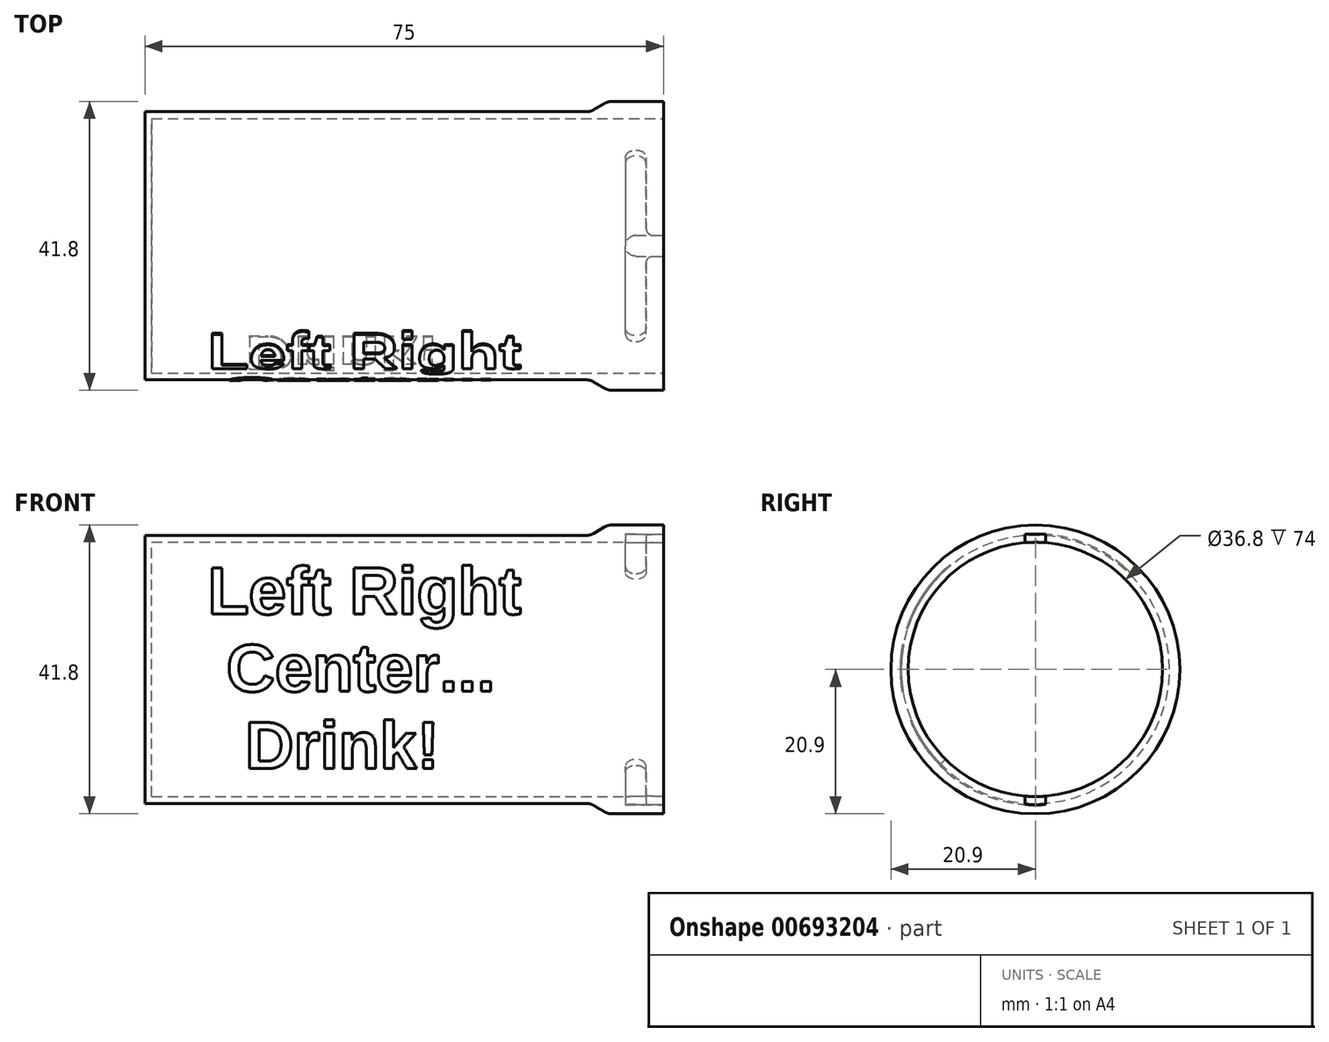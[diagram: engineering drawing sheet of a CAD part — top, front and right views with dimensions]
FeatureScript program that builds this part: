
annotation { "Feature Type Name" : "Feature", "Feature Type Description" : "" }
export const myFeature = defineFeature(function(context is Context, id is Id, definition is map)
    precondition{}
    {
        {
            var Q0;
            Q0=qCreatedBy(makeId("Front.planeOp"),FACE);
            var sketch = newSketch(context, id + "F0", { "sketchPlane" : qUnion([Q0])});
            skLineSegment(sketch, "E0", {"start": v(0, 0) * mm, "end": v(0, 19.4) * mm});
            skLineSegment(sketch, "E1", {"start": v(0, 19.4) * mm, "end": v(64.4, 19.4) * mm});
            skLineSegment(sketch, "E2", {"start": v(67, 20.9) * mm, "end": v(75, 20.9) * mm});
            skLineSegment(sketch, "E3", {"start": v(75, 20.9) * mm, "end": v(75, 18.4) * mm});
            skLineSegment(sketch, "E4", {"start": v(68.5, 18.4) * mm, "end": v(1, 18.4) * mm});
            skLineSegment(sketch, "E5", {"start": v(1, 18.4) * mm, "end": v(1, 0) * mm});
            skLineSegment(sketch, "E6", {"start": v(1, 0) * mm, "end": v(0, 0) * mm});
            skLineSegment(sketch, "E7", {"start": v(68.5, 18.4) * mm, "end": v(75, 18.4) * mm});
            skLineSegment(sketch, "E8", {"start": v(67, 20.9) * mm, "end": v(64.4, 19.4) * mm});
            skSolve(sketch);
        }
        {
            var Q0;
            Q0=makeQuery(id+"F0.imprint","IMPRINT",FACE,{"disambiguationData":[TD([[makeQuery(id+"F0.imprint","IMPRINT",EDGE,{"derivedFrom":sQuery(id+"F0.wireOp",EDGE,"E0")}),-1.0]])]});
            var Q1;
            Q1=sQuery(id+"F0.wireOp",EDGE,"E6");
            revolve(context, id + "F1", {"surfaceOperationType" : NewSurfaceOperationType.NEW, "entities" : qUnion([Q0]), "axis" : qUnion([Q1]), "revolveType" : RevolveType.FULL});
        }
        {
            var Q0;
            Q0=makeQuery(id+"F1.opRevolve","SWEPT_EDGE",EDGE,{"disambiguationData":[OSD([sQuery(id+"F0.wireOp",EDGE,"E2"),sQuery(id+"F0.wireOp",EDGE,"E8")])]});
            var Q1;
            Q1=makeQuery(id+"F1.opRevolve","SWEPT_EDGE",EDGE,{"disambiguationData":[OSD([sQuery(id+"F0.wireOp",EDGE,"E1"),sQuery(id+"F0.wireOp",EDGE,"E8")])]});
            fillet(context, id + "F2", {"entities" : qUnion([Q0, Q1]), "radius" : 2 * mm, "tangentPropagation" : true, "allowEdgeOverflow" : false});
        }
        {
            var Q0;
            Q0=makeQuery(id+"F1.opRevolve","SWEPT_FACE",FACE,{"disambiguationData":[OSD([sQuery(id+"F0.wireOp",EDGE,"E3")])]});
            var sketch = newSketch(context, id + "F3", { "sketchPlane" : qUnion([Q0])});
            skLineSegment(sketch, "E9.left", {"start": v(1.5, 19.54) * mm, "end": v(1.5, -19.54) * mm});
            skLineSegment(sketch, "E9.right", {"start": v(-1.5, 19.54) * mm, "end": v(-1.5, -19.54) * mm});
            skPoint(sketch, "E9.middle", {"position": v(0, 0) * mm});
            skArc(sketch, "E10", {"start": v(1.5, 19.54) * mm, "mid": v(0, 19.6) * mm, "end": v(-1.5, 19.54) * mm});
            skArc(sketch, "E11.trimOffspring", {"start": v(-1.5, -19.54) * mm, "mid": v(0, -19.6) * mm, "end": v(1.5, -19.54) * mm});
            skSolve(sketch);
        }
        {
            var Q0;
            Q0=qSketchRegion(id+"F3",true);
            extrude(context, id + "F4", {"entities" : qUnion([Q0]), "operationType" : NewBodyOperationType.REMOVE, "oppositeDirection" : true, "depth" : 5.5 * mm, "offsetDistance" : 25 * mm});
        }
        {
            var Q0;
            Q0=qCreatedBy(makeId("Front.planeOp"),FACE);
            var sketch = newSketch(context, id + "F5", { "sketchPlane" : qUnion([Q0])});
            skLineSegment(sketch, "E12.bottom", {"start": v(72.5, 19.6) * mm, "end": v(69.5, 19.6) * mm});
            skLineSegment(sketch, "E12.left", {"start": v(72.5, 19.6) * mm, "end": v(72.5, 0) * mm});
            skLineSegment(sketch, "E12.right", {"start": v(69.5, 19.6) * mm, "end": v(69.5, 0) * mm});
            skPoint(sketch, "E12.middle", {"position": v(74.25, 0) * mm});
            skLineSegment(sketch, "E13", {"start": v(69.5, 0) * mm, "end": v(72.5, 0) * mm, "construction": true});
            skLineSegment(sketch, "E14", {"start": v(69.5, 12.25) * mm, "end": v(72.5, 12.25) * mm});
            skSolve(sketch);
        }
        {
            var Q0;
            {var subQ0=sQuery(id+"F5.wireOp",EDGE,"E12.bottom");Q0=makeQuery(id+"F5.imprint","IMPRINT",FACE,{"disambiguationData":[TD([[makeQuery(id+"F5.imprint","IMPRINT",EDGE,{"derivedFrom":subQ0}),1.0]])]});}
            var Q1;
            Q1=sQuery(id+"F5.wireOp",EDGE,"E13");
            revolve(context, id + "F6", {"operationType" : NewBodyOperationType.REMOVE, "surfaceOperationType" : NewSurfaceOperationType.NEW, "entities" : qUnion([Q0]), "axis" : qUnion([Q1]), "revolveType" : RevolveType.ONE_DIRECTION, "oppositeDirection" : true, "angle" : 45 * degree});
        }
        {
            var Q0;
            Q0=qCreatedBy(makeId("Front.planeOp"),FACE);
            var sketch = newSketch(context, id + "F7", { "sketchPlane" : qUnion([Q0])});
            skLineSegment(sketch, "E15.bottom", {"start": v(72.5, -19.6) * mm, "end": v(69.5, -19.6) * mm});
            skLineSegment(sketch, "E15.top", {"start": v(72.5, 0) * mm, "end": v(69.5, 0) * mm, "construction": true});
            skLineSegment(sketch, "E15.left", {"start": v(72.5, -19.6) * mm, "end": v(72.5, 0) * mm});
            skLineSegment(sketch, "E15.right", {"start": v(69.5, -19.6) * mm, "end": v(69.5, 0) * mm});
            skLineSegment(sketch, "E16", {"start": v(72.5, -11.28) * mm, "end": v(69.5, -11.28) * mm});
            skSolve(sketch);
        }
        {
            var Q0;
            {var subQ0=sQuery(id+"F7.wireOp",EDGE,"E15.bottom");Q0=makeQuery(id+"F7.imprint","IMPRINT",FACE,{"disambiguationData":[TD([[makeQuery(id+"F7.imprint","IMPRINT",EDGE,{"derivedFrom":subQ0}),-1.0]])]});}
            var Q1;
            Q1=sQuery(id+"F7.wireOp",EDGE,"E15.top");
            revolve(context, id + "F8", {"operationType" : NewBodyOperationType.REMOVE, "surfaceOperationType" : NewSurfaceOperationType.NEW, "entities" : qUnion([Q0]), "axis" : qUnion([Q1]), "revolveType" : RevolveType.ONE_DIRECTION, "angle" : 45 * degree});
        }
        {
            var Q0;
            {var subQ0=sQuery(id+"F3.wireOp",EDGE,"E9.right");var subQ1=sQuery(id+"F3.wireOp",EDGE,"E10");Q0=makeQuery(id+"F4.boolean.opBoolean","COPY",EDGE,{"disambiguationData":[TD([makeQuery(id+"F4.opExtrude","SWEPT_FACE",FACE,{"disambiguationData":[OSD([subQ1])]})])],"derivedFrom":makeQuery(id+"F4.opExtrude","CAP_EDGE",EDGE,{"disambiguationData":[OSD([subQ0])],"isStart":false})});}
            var Q1;
            {var subQ0=sQuery(id+"F3.wireOp",EDGE,"E9.left");var subQ1=sQuery(id+"F3.wireOp",EDGE,"E11.trimOffspring");Q1=makeQuery(id+"F4.boolean.opBoolean","COPY",EDGE,{"disambiguationData":[TD([makeQuery(id+"F4.opExtrude","SWEPT_FACE",FACE,{"disambiguationData":[OSD([subQ1])]})])],"derivedFrom":makeQuery(id+"F4.opExtrude","CAP_EDGE",EDGE,{"disambiguationData":[OSD([subQ0])],"isStart":false})});}
            fillet(context, id + "F9", {"entities" : qUnion([Q0, Q1]), "radius" : 1.5 * mm, "tangentPropagation" : true, "allowEdgeOverflow" : false});
        }
        {
            var Q0;
            Q0=makeQuery(id+"F6.boolean.opBoolean","COPY",EDGE,{"derivedFrom":makeQuery(id+"F6.opRevolve","CAP_EDGE",EDGE,{"disambiguationData":[OSD([sQuery(id+"F5.wireOp",EDGE,"E12.right")])],"isStart":false})});
            var Q1;
            Q1=makeQuery(id+"F6.boolean.opBoolean","COPY",EDGE,{"derivedFrom":makeQuery(id+"F6.opRevolve","CAP_EDGE",EDGE,{"disambiguationData":[OSD([sQuery(id+"F5.wireOp",EDGE,"E12.left")])],"isStart":false})});
            var Q2;
            Q2=makeQuery(id+"F8.boolean.opBoolean","COPY",EDGE,{"derivedFrom":makeQuery(id+"F8.opRevolve","CAP_EDGE",EDGE,{"disambiguationData":[OSD([sQuery(id+"F7.wireOp",EDGE,"E15.right")])],"isStart":false})});
            var Q3;
            Q3=makeQuery(id+"F8.boolean.opBoolean","COPY",EDGE,{"derivedFrom":makeQuery(id+"F8.opRevolve","CAP_EDGE",EDGE,{"disambiguationData":[OSD([sQuery(id+"F7.wireOp",EDGE,"E15.left")])],"isStart":false})});
            fillet(context, id + "F10", {"entities" : qUnion([Q0, Q1, Q2, Q3]), "radius" : 1.5 * mm, "tangentPropagation" : true, "allowEdgeOverflow" : false});
        }
        {
            var Q0;
            {var subQ0=sQuery(id+"F3.wireOp",EDGE,"E10");var subQ1=sQuery(id+"F3.wireOp",EDGE,"E9.left");Q0=makeQuery(id+"F6.boolean.opBoolean","INTERSECT",EDGE,{"derivedFrom":[makeQuery(id+"F4.boolean.opBoolean","COPY",FACE,{"disambiguationData":[TD([makeQuery(id+"F4.opExtrude","SWEPT_FACE",FACE,{"disambiguationData":[OSD([subQ0])]})])],"derivedFrom":makeQuery(id+"F4.opExtrude","SWEPT_FACE",FACE,{"disambiguationData":[OSD([subQ1])]})}),makeQuery(id+"F6.opRevolve","SWEPT_FACE",FACE,{"disambiguationData":[OSD([sQuery(id+"F5.wireOp",EDGE,"E12.left")])]})]});}
            var Q1;
            {var subQ0=sQuery(id+"F3.wireOp",EDGE,"E11.trimOffspring");var subQ1=sQuery(id+"F3.wireOp",EDGE,"E9.right");Q1=makeQuery(id+"F8.boolean.opBoolean","INTERSECT",EDGE,{"derivedFrom":[makeQuery(id+"F4.boolean.opBoolean","COPY",FACE,{"disambiguationData":[TD([makeQuery(id+"F4.opExtrude","SWEPT_FACE",FACE,{"disambiguationData":[OSD([subQ0])]})])],"derivedFrom":makeQuery(id+"F4.opExtrude","SWEPT_FACE",FACE,{"disambiguationData":[OSD([subQ1])]})}),makeQuery(id+"F8.opRevolve","SWEPT_FACE",FACE,{"disambiguationData":[OSD([sQuery(id+"F7.wireOp",EDGE,"E15.left")])]})]});}
            fillet(context, id + "F11", {"entities" : qUnion([Q0, Q1]), "radius" : 1 * mm, "tangentPropagation" : true, "allowEdgeOverflow" : false});
        }
        {
            var Q0;
            Q0=qCreatedBy(makeId("Right.planeOp"),FACE);
            var sketch = newSketch(context, id + "F12", { "sketchPlane" : qUnion([Q0])});
            skLineSegment(sketch, "E17", {"start": v(0, 19.88) * mm, "end": v(0, -19.8) * mm});
            skLineSegment(sketch, "E18", {"start": v(0, 19.88) * mm, "end": v(29.27, 19.88) * mm});
            skLineSegment(sketch, "E19", {"start": v(29.27, 19.88) * mm, "end": v(29.27, -21.23) * mm});
            skLineSegment(sketch, "E20", {"start": v(29.27, -21.23) * mm, "end": v(0, -19.8) * mm});
            skSolve(sketch);
        }
        {
            var Q0;
            Q0=qCreatedBy(makeId("Front.planeOp"),FACE);
            var sketch = newSketch(context, id + "F13", { "sketchPlane" : qUnion([Q0])});
            skText(sketch, "E21", { "text": "Left Right \n Center...\n  Drink!", "fontName": "Arimo-Bold.ttf"});
            skLineSegment(sketch, "E22", {"start": v(32.04, 8) * mm, "end": v(32.04, 0) * mm, "construction": true});
            skLineSegment(sketch, "E23", {"start": v(9.09, 11.5) * mm, "end": v(0, 11.5) * mm});
            skLineSegment(sketch, "E24", {"start": v(55, 11.5) * mm, "end": v(75, 11.5) * mm});
            const initialGuessF13  = {"E21": [0.00909, 0.008, 1, 0, 0.007]};
            skSetInitialGuess(sketch, initialGuessF13);
            skSolve(sketch);
        }
        {
            var Q0;
            Q0=qSketchRegion(id+"F13",true);
            extrude(context, id + "F14", {"entities" : qUnion([Q0]), "operationType" : NewBodyOperationType.ADD, "depth" : 20 * mm, "offsetDistance" : 25 * mm});
        }
        {
            var Q0;
            Q0=makeQuery(id+"F1.opRevolve","SWEPT_FACE",FACE,{"disambiguationData":[OSD([sQuery(id+"F0.wireOp",EDGE,"E0")])]});
            var sketch = newSketch(context, id + "F15", { "sketchPlane" : qUnion([Q0])});
            skCircle(sketch, "E25.0", {"center": v(0, 0) * mm, "radius": 19.5 * mm});
            skCircle(sketch, "E26.0", {"center": v(0, 0) * mm, "radius": 29.5 * mm});
            skSolve(sketch);
        }
        {
            var Q0;
            Q0=qSketchRegion(id+"F15",true);
            extrude(context, id + "F16", {"entities" : qUnion([Q0]), "operationType" : NewBodyOperationType.REMOVE, "oppositeDirection" : true, "depth" : 61.2 * mm, "offsetDistance" : 25 * mm});
        }
        {
            var Q0;
            Q0=makeQuery(id+"F1.opRevolve","SWEPT_FACE",FACE,{"disambiguationData":[OSD([sQuery(id+"F0.wireOp",EDGE,"E5")])]});
            extrude(context, id + "F17", {"entities" : qUnion([Q0]), "operationType" : NewBodyOperationType.REMOVE, "endBound" : BoundingType.THROUGH_ALL, "depth" : 25 * mm, "offsetDistance" : 25 * mm});
        }
    });
